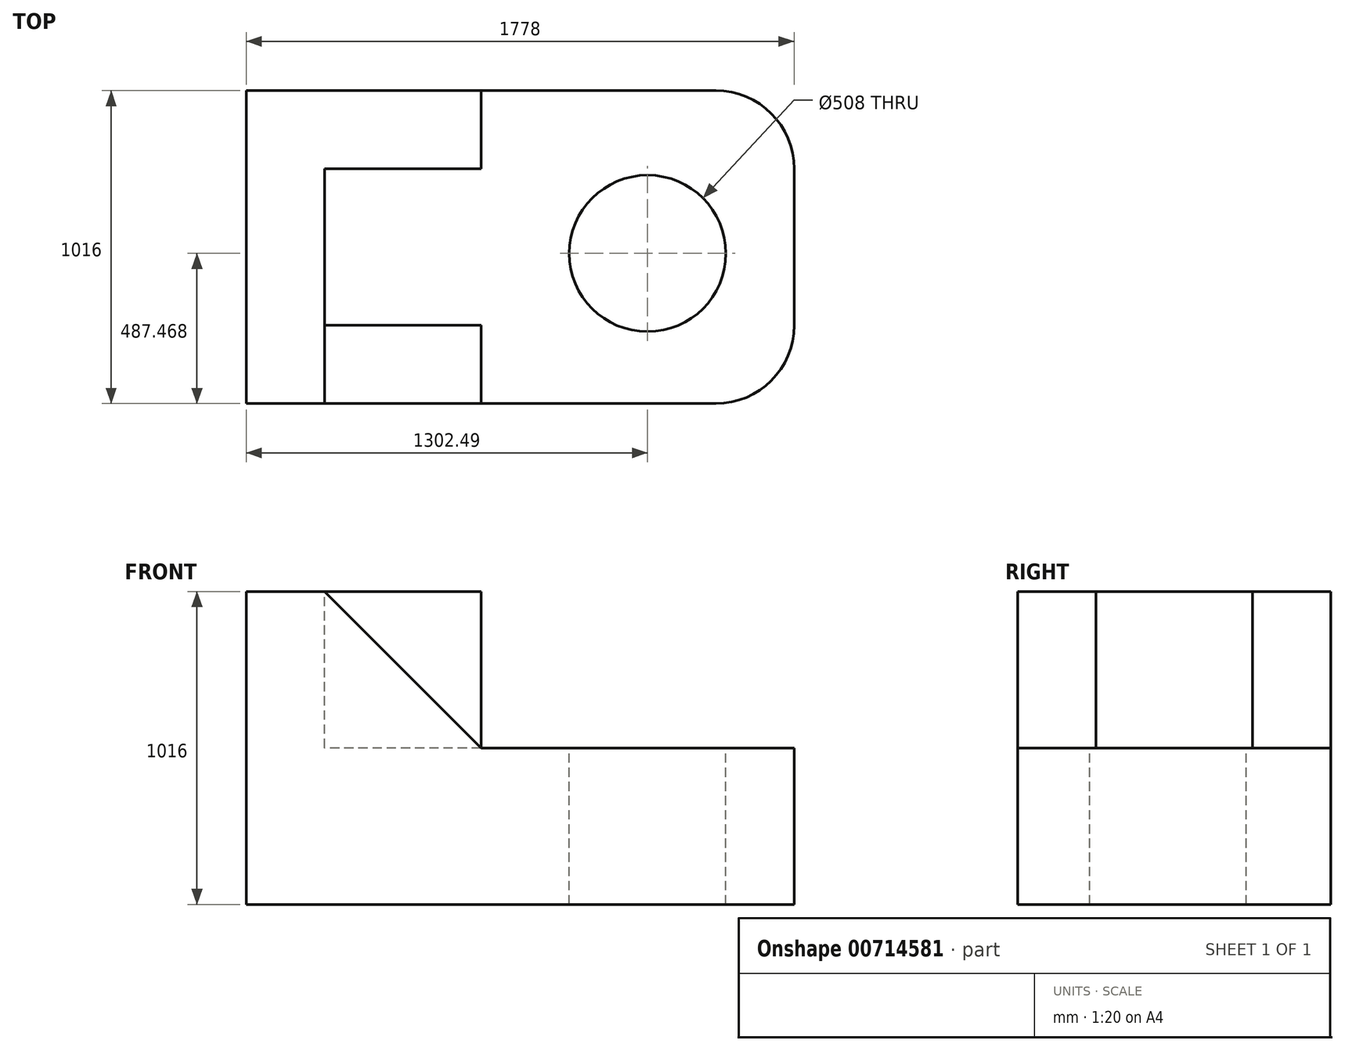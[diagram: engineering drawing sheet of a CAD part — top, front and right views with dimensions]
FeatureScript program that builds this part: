
annotation { "Feature Type Name" : "Feature", "Feature Type Description" : "" }
export const myFeature = defineFeature(function(context is Context, id is Id, definition is map)
    precondition{}
    {
        {
            var Q0;
            Q0=qCreatedBy(makeId("Top.planeOp"),FACE);
            var sketch = newSketch(context, id + "F0", { "sketchPlane" : qUnion([Q0])});
            skLineSegment(sketch, "E0.bottom", {"start": v(0, 0) * mm, "end": v(1778, 0) * mm});
            skLineSegment(sketch, "E0.top", {"start": v(0, 1016) * mm, "end": v(1778, 1016) * mm});
            skLineSegment(sketch, "E0.left", {"start": v(0, 0) * mm, "end": v(0, 1016) * mm});
            skLineSegment(sketch, "E0.right", {"start": v(1778, 0) * mm, "end": v(1778, 1016) * mm});
            skSolve(sketch);
        }
        {
            var Q0;
            Q0=makeQuery(id+"F0.imprint","IMPRINT",FACE,{"disambiguationData":[TD([[makeQuery(id+"F0.imprint","IMPRINT",EDGE,{"derivedFrom":sQuery(id+"F0.wireOp",EDGE,"E0.bottom")}),1.0]])]});
            extrude(context, id + "F1", {"entities" : qUnion([Q0]), "depth" : 1016 * mm, "offsetDistance" : 25.4 * mm});
        }
        {
            var Q0;
            Q0=makeQuery(id+"F1.opExtrude","CAP_FACE",FACE,{"disambiguationData":[OSD([sQuery(id+"F0.wireOp",EDGE,"E0.bottom"),sQuery(id+"F0.wireOp",EDGE,"E0.top"),sQuery(id+"F0.wireOp",EDGE,"E0.left"),sQuery(id+"F0.wireOp",EDGE,"E0.right")])],"isStart":false});
            var sketch = newSketch(context, id + "F2", { "sketchPlane" : qUnion([Q0])});
            skLineSegment(sketch, "E1", {"start": v(0, 1016) * mm, "end": v(762, 1016) * mm});
            skLineSegment(sketch, "E2", {"start": v(762, 1016) * mm, "end": v(762, 762) * mm});
            skLineSegment(sketch, "E3", {"start": v(762, 762) * mm, "end": v(254, 762) * mm});
            skLineSegment(sketch, "E4", {"start": v(254, 762) * mm, "end": v(254, 254) * mm});
            skLineSegment(sketch, "E5", {"start": v(254, 254) * mm, "end": v(762, 254) * mm});
            skLineSegment(sketch, "E6", {"start": v(762, 254) * mm, "end": v(762, 0) * mm});
            skSolve(sketch);
        }
        {
            var Q0;
            {var subQ0=sQuery(id+"F2.wireOp",EDGE,"E2");Q0=makeQuery(id+"F2.imprint","IMPRINT",FACE,{"disambiguationData":[TD([[makeQuery(id+"F2.imprint","IMPRINT",EDGE,{"derivedFrom":subQ0}),1.0]])]});}
            extrude(context, id + "F3", {"entities" : qUnion([Q0]), "operationType" : NewBodyOperationType.REMOVE, "oppositeDirection" : true, "depth" : 508 * mm, "offsetDistance" : 25.4 * mm});
        }
        {
            var Q0;
            Q0=makeQuery(id+"F1.opExtrude","CAP_FACE",FACE,{"disambiguationData":[OSD([sQuery(id+"F0.wireOp",EDGE,"E0.bottom"),sQuery(id+"F0.wireOp",EDGE,"E0.top"),sQuery(id+"F0.wireOp",EDGE,"E0.left"),sQuery(id+"F0.wireOp",EDGE,"E0.right")])],"isStart":false});
            var sketch = newSketch(context, id + "F4", { "sketchPlane" : qUnion([Q0])});
            skLineSegment(sketch, "E7", {"start": v(254, 254) * mm, "end": v(254, 0) * mm});
            skSolve(sketch);
        }
        {
            var Q0;
            Q0=makeQuery(id+"F1.opExtrude","SWEPT_FACE",FACE,{"disambiguationData":[OSD([sQuery(id+"F0.wireOp",EDGE,"E0.bottom")])]});
            var sketch = newSketch(context, id + "F5", { "sketchPlane" : qUnion([Q0])});
            skLineSegment(sketch, "E8", {"start": v(254, 1016) * mm, "end": v(762, 508) * mm});
            skSolve(sketch);
        }
        {
            var Q0;
            {var subQ0=sQuery(id+"F5.wireOp",EDGE,"E8");Q0=makeQuery(id+"F5.imprint","IMPRINT",FACE,{"disambiguationData":[TD([[makeQuery(id+"F5.imprint","IMPRINT",EDGE,{"derivedFrom":subQ0}),1.0]])]});}
            extrude(context, id + "F6", {"entities" : qUnion([Q0]), "operationType" : NewBodyOperationType.REMOVE, "oppositeDirection" : true, "depth" : 254 * mm, "offsetDistance" : 25.4 * mm});
        }
        {
            var Q0;
            {var subQ0=sQuery(id+"F4.wireOp",EDGE,"E7");Q0=makeQuery(id+"F4.imprint","IMPRINT",FACE,{"disambiguationData":[TD([[makeQuery(id+"F4.imprint","IMPRINT",EDGE,{"derivedFrom":subQ0}),1.0]])]});}
            extrude(context, id + "F7", {"entities" : qUnion([Q0]), "operationType" : NewBodyOperationType.REMOVE, "depth" : 175.26 * mm, "offsetDistance" : 25.4 * mm});
        }
        {
            var Q0;
            Q0=makeQuery(id+"F3.boolean.opBoolean","COPY",FACE,{"derivedFrom":makeQuery(id+"F3.opExtrude","CAP_FACE",FACE,{"disambiguationData":[OSD([sQuery(id+"F0.wireOp",EDGE,"E0.bottom"),sQuery(id+"F0.wireOp",EDGE,"E0.top"),sQuery(id+"F0.wireOp",EDGE,"E0.right"),sQuery(id+"F2.wireOp",EDGE,"E2"),sQuery(id+"F2.wireOp",EDGE,"E3"),sQuery(id+"F2.wireOp",EDGE,"E4"),sQuery(id+"F2.wireOp",EDGE,"E5"),sQuery(id+"F2.wireOp",EDGE,"E6")])],"isStart":false})});
            var sketch = newSketch(context, id + "F8", { "sketchPlane" : qUnion([Q0])});
            skCircle(sketch, "E9", {"center": v(1302.5, 487.47) * mm, "radius": 254 * mm});
            skSolve(sketch);
        }
        {
            var Q0;
            Q0=makeQuery(id+"F8.imprint","IMPRINT",FACE,{"disambiguationData":[TD([[makeQuery(id+"F8.imprint","IMPRINT",EDGE,{"derivedFrom":sQuery(id+"F8.wireOp",EDGE,"E9")}),1.0]])]});
            extrude(context, id + "F9", {"entities" : qUnion([Q0]), "operationType" : NewBodyOperationType.REMOVE, "oppositeDirection" : true, "depth" : 508 * mm, "offsetDistance" : 25.4 * mm});
        }
        {
            var Q0;
            Q0=makeQuery(id+"F1.opExtrude","SWEPT_EDGE",EDGE,{"disambiguationData":[OSD([sQuery(id+"F0.wireOp",EDGE,"E0.bottom"),sQuery(id+"F0.wireOp",EDGE,"E0.right")])]});
            fillet(context, id + "F10", {"entities" : qUnion([Q0]), "radius" : 254 * mm, "tangentPropagation" : true, "allowEdgeOverflow" : false});
        }
        {
            var Q0;
            Q0=makeQuery(id+"F1.opExtrude","SWEPT_EDGE",EDGE,{"disambiguationData":[OSD([sQuery(id+"F0.wireOp",EDGE,"E0.top"),sQuery(id+"F0.wireOp",EDGE,"E0.right")])]});
            fillet(context, id + "F11", {"entities" : qUnion([Q0]), "radius" : 254 * mm, "tangentPropagation" : true, "allowEdgeOverflow" : false});
        }
    });
